# Revit family: Sanitary_Taps-mixers_hansgrohe_74420XXX-Zesis-S-Single-lever-bath-mixer-set_exposed-installation
name_source: partatom
category: Plumbing Fixtures
units: mm (PartAtom-declared; Revit-internal decimal feet)

## family parameters
Always vertical = No
Cut with Voids When Loaded = No
Maintain Annotation Orientation = No
OmniClass Number = 23.31.11.00
OmniClass Title = Faucets
Part Type = Normal
Room Calculation Point = No
Round Connector Dimension = Use Diameter
Shared = No
Work Plane-Based = Yes

## types (2) — shared parameters
Connector Description 1 = Water Inlet 12.7 mm
Connector Description 2 = Water Outlet 12.7 mm
Default Elevation = 1219 mm
Description = Zesis S Single lever bath mixer for exposed installation
Diameter = 13 mm
Manufacturer = Hansgrohe
Model = 74420XXX
Product Page URL = https://www.hansgrohe.com
Product data url = https://www.bimobject.com
URL = https://www.hansgrohe.com
Version = 1

## per-type parameters (varying)
| type | Product Material |
| 000 Chrome | Hansgrohe - Metal - 000 Chrome |
| 670 Matt Black | Hansgrohe - Metal - 670 Matte Black |

## geometry (parser evidence)
native form markers: Sweep x3
no freeform markers — native parametric forms only
